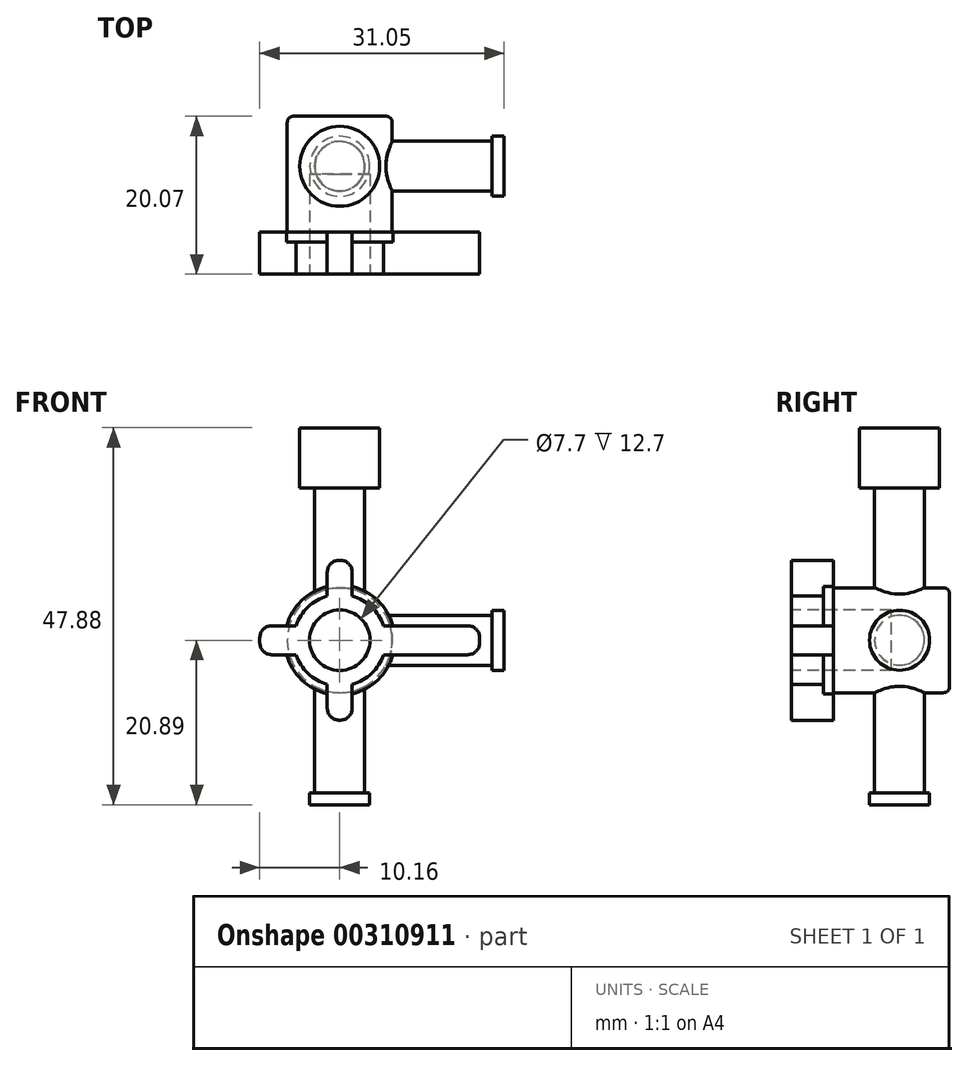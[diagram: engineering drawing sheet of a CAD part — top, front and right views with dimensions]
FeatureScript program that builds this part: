
annotation { "Feature Type Name" : "Feature", "Feature Type Description" : "" }
export const myFeature = defineFeature(function(context is Context, id is Id, definition is map)
    precondition{}
    {
        {
            var Q0;
            Q0=qCreatedBy(makeId("Front.planeOp"),FACE);
            var sketch = newSketch(context, id + "F0", { "sketchPlane" : qUnion([Q0])});
            skCircle(sketch, "E0", {"center": v(0, 0) * mm, "radius": 6.67 * mm});
            skSolve(sketch);
        }
        {
            var Q0;
            Q0 = qSketchRegion(id + "F0", true);
            extrude(context, id + "F1", {"entities" : qUnion([Q0]), "depth" : 14.73 * mm});
        }
        {
            var Q0;
            Q0=qCreatedBy(makeId("Top.planeOp"),FACE);
            var sketch = newSketch(context, id + "F2", { "sketchPlane" : qUnion([Q0])});
            skCircle(sketch, "E1", {"center": v(0, -6.35) * mm, "radius": 3.18 * mm});
            skSolve(sketch);
        }
        {
            var Q0;
            Q0 = qSketchRegion(id + "F2", true);
            extrude(context, id + "F3", {"entities" : qUnion([Q0]), "operationType" : NewBodyOperationType.ADD, "endBound" : BoundingType.SYMMETRIC, "depth" : 38.73 * mm});
        }
        {
            var Q0;
            Q0=qCreatedBy(makeId("Right.planeOp"),FACE);
            var sketch = newSketch(context, id + "F4", { "sketchPlane" : qUnion([Q0])});
            skCircle(sketch, "E2", {"center": v(-6.35, 0) * mm, "radius": 3.18 * mm});
            skSolve(sketch);
        }
        {
            var Q0;
            Q0 = qSketchRegion(id + "F4", true);
            extrude(context, id + "F5", {"entities" : qUnion([Q0]), "operationType" : NewBodyOperationType.ADD, "depth" : 19.37 * mm});
        }
        {
            var Q0;
            Q0=makeQuery(id+"F1.opExtrude","CAP_EDGE",EDGE,{"disambiguationData":[OSD([sQuery(id+"F0.wireOp",EDGE,"E0")])],"isStart":true});
            fillet(context, id + "F6", {"entities" : qUnion([Q0]), "radius" : 0.76 * mm, "tangentPropagation" : true, "allowEdgeOverflow" : false});
        }
        {
            var Q0;
            Q0=makeQuery(id+"F3.opExtrude","CAP_FACE",FACE,{"disambiguationData":[OSD([sQuery(id+"F2.wireOp",EDGE,"E1")])],"isStart":false});
            var sketch = newSketch(context, id + "F7", { "sketchPlane" : qUnion([Q0])});
            skCircle(sketch, "E3", {"center": v(0, -6.35) * mm, "radius": 5.08 * mm});
            skSolve(sketch);
        }
        {
            var Q0;
            Q0 = qSketchRegion(id + "F7", true);
            extrude(context, id + "F8", {"entities" : qUnion([Q0]), "operationType" : NewBodyOperationType.ADD, "depth" : 7.62 * mm});
        }
        {
            var Q0;
            Q0=makeQuery(id+"F5.opExtrude","CAP_FACE",FACE,{"disambiguationData":[OSD([sQuery(id+"F4.wireOp",EDGE,"E2")])],"isStart":false});
            var sketch = newSketch(context, id + "F9", { "sketchPlane" : qUnion([Q0])});
            skCircle(sketch, "E4", {"center": v(-6.35, 0) * mm, "radius": 3.81 * mm});
            skSolve(sketch);
        }
        {
            var Q0;
            Q0 = qSketchRegion(id + "F9", true);
            extrude(context, id + "F10", {"entities" : qUnion([Q0]), "operationType" : NewBodyOperationType.ADD, "depth" : 1.52 * mm});
        }
        {
            var Q0;
            Q0=makeQuery(id+"F3.opExtrude","CAP_FACE",FACE,{"disambiguationData":[OSD([sQuery(id+"F2.wireOp",EDGE,"E1")])],"isStart":true});
            var sketch = newSketch(context, id + "F11", { "sketchPlane" : qUnion([Q0])});
            skCircle(sketch, "E5", {"center": v(0, 6.35) * mm, "radius": 3.81 * mm});
            skSolve(sketch);
        }
        {
            var Q0;
            Q0 = qSketchRegion(id + "F11", true);
            extrude(context, id + "F12", {"entities" : qUnion([Q0]), "operationType" : NewBodyOperationType.ADD, "depth" : 1.52 * mm});
        }
        {
            var Q0;
            Q0=makeQuery(id+"F1.opExtrude","CAP_FACE",FACE,{"disambiguationData":[OSD([sQuery(id+"F0.wireOp",EDGE,"E0")])],"isStart":false});
            var sketch = newSketch(context, id + "F13", { "sketchPlane" : qUnion([Q0])});
            skCircle(sketch, "E6", {"center": v(0, 0) * mm, "radius": 6.99 * mm});
            skSolve(sketch);
        }
        {
            var Q0;
            Q0 = qSketchRegion(id + "F13", true);
            extrude(context, id + "F14", {"entities" : qUnion([Q0]), "depth" : 1.27 * mm});
        }
        {
            var Q0;
            Q0=makeQuery(id+"F14.opExtrude","CAP_FACE",FACE,{"disambiguationData":[OSD([sQuery(id+"F13.wireOp",EDGE,"E6")])],"isStart":false});
            var sketch = newSketch(context, id + "F15", { "sketchPlane" : qUnion([Q0])});
            skCircle(sketch, "E7", {"center": v(0, 0) * mm, "radius": 5.84 * mm});
            skCircle(sketch, "E8", {"center": v(0, 0) * mm, "radius": 3.81 * mm});
            skSolve(sketch);
        }
        {
            var Q0;
            Q0 = qSketchRegion(id + "F15", true);
            extrude(context, id + "F16", {"entities" : qUnion([Q0]), "operationType" : NewBodyOperationType.ADD, "depth" : 4.06 * mm});
        }
        {
            var Q0;
            Q0=makeQuery(id+"F14.opExtrude","CAP_FACE",FACE,{"disambiguationData":[OSD([sQuery(id+"F13.wireOp",EDGE,"E6")])],"isStart":true});
            var sketch = newSketch(context, id + "F17", { "sketchPlane" : qUnion([Q0])});
            skLineSegment(sketch, "E9.bottom", {"start": v(1.59, 10.16) * mm, "end": v(-1.59, 10.16) * mm});
            skLineSegment(sketch, "E9.top", {"start": v(1.59, -10.16) * mm, "end": v(-1.59, -10.16) * mm});
            skLineSegment(sketch, "E9.left", {"start": v(1.59, 10.16) * mm, "end": v(1.59, -10.16) * mm});
            skLineSegment(sketch, "E9.right", {"start": v(-1.59, 10.16) * mm, "end": v(-1.59, -10.16) * mm});
            skPoint(sketch, "E9.middle", {"position": v(0, 0) * mm});
            skSolve(sketch);
        }
        {
            var Q0;
            Q0 = qSketchRegion(id + "F17", true);
            var Q1;
            Q1=makeQuery(id+"F16.opExtrude","CAP_FACE",FACE,{"disambiguationData":[OSD([sQuery(id+"F15.wireOp",EDGE,"E7"),sQuery(id+"F15.wireOp",EDGE,"E8")])],"isStart":false});
            extrude(context, id + "F18", {"entities" : qUnion([Q0]), "operationType" : NewBodyOperationType.ADD, "endBound" : BoundingType.UP_TO_SURFACE, "oppositeDirection" : true, "endBoundEntityFace" : qUnion([Q1]), "depth" : 25.4 * mm});
        }
        {
            var Q0;
            Q0=makeQuery(id+"F18.boolean.opBoolean","MERGE",FACE,{"derivedFrom":[makeQuery(id+"F14.opExtrude","CAP_FACE",FACE,{"disambiguationData":[OSD([sQuery(id+"F13.wireOp",EDGE,"E6")])],"isStart":true}),makeQuery(id+"F18.opExtrude","CAP_FACE",FACE,{"disambiguationData":[OSD([sQuery(id+"F17.wireOp",EDGE,"E9.bottom"),sQuery(id+"F17.wireOp",EDGE,"E9.top"),sQuery(id+"F17.wireOp",EDGE,"E9.left"),sQuery(id+"F17.wireOp",EDGE,"E9.right")])],"isStart":true})]});
            var sketch = newSketch(context, id + "F19", { "sketchPlane" : qUnion([Q0])});
            skLineSegment(sketch, "E10.bottom", {"start": v(-17.78, 1.84) * mm, "end": v(10.16, 1.84) * mm});
            skLineSegment(sketch, "E10.top", {"start": v(-17.78, -1.84) * mm, "end": v(10.16, -1.84) * mm});
            skLineSegment(sketch, "E10.left", {"start": v(-17.78, 1.84) * mm, "end": v(-17.78, -1.84) * mm});
            skLineSegment(sketch, "E10.right", {"start": v(10.16, 1.84) * mm, "end": v(10.16, -1.84) * mm});
            skPoint(sketch, "E10.middle", {"position": v(-3.81, 0) * mm});
            skPoint(sketch, "E10.middle.positionSnap0", {"position": v(-6.99, 0) * mm});
            skPoint(sketch, "E10.centerSnap0", {"position": v(-6.99, 0) * mm});
            skSolve(sketch);
        }
        {
            var Q0;
            Q0 = qSketchRegion(id + "F19", true);
            var Q1;
            {var subQ0=sQuery(id+"F15.wireOp",EDGE,"E8");var subQ1=sQuery(id+"F15.wireOp",EDGE,"E7");Q1=makeQuery(id+"F18.boolean.opBoolean","MERGE",FACE,{"derivedFrom":[makeQuery(id+"F16.opExtrude","CAP_FACE",FACE,{"disambiguationData":[OSD([subQ1,subQ0])],"isStart":false}),makeQuery(id+"F18.opExtrude","CAP_FACE",FACE,{"disambiguationData":[OSD([subQ1,subQ0])],"isStart":false})]});}
            extrude(context, id + "F20", {"entities" : qUnion([Q0]), "operationType" : NewBodyOperationType.ADD, "endBound" : BoundingType.UP_TO_SURFACE, "oppositeDirection" : true, "endBoundEntityFace" : qUnion([Q1]), "depth" : 25.4 * mm});
        }
        {
            var Q0;
            {var subQ0=sQuery(id+"F15.wireOp",EDGE,"E8");var subQ1=sQuery(id+"F15.wireOp",EDGE,"E7");Q0=makeQuery(id+"F20.boolean.opBoolean","MERGE",FACE,{"derivedFrom":[makeQuery(id+"F18.boolean.opBoolean","MERGE",FACE,{"derivedFrom":[makeQuery(id+"F16.opExtrude","CAP_FACE",FACE,{"disambiguationData":[OSD([subQ1,subQ0])],"isStart":false}),makeQuery(id+"F18.opExtrude","CAP_FACE",FACE,{"disambiguationData":[OSD([subQ1,subQ0])],"isStart":false})]}),makeQuery(id+"F20.opExtrude","CAP_FACE",FACE,{"disambiguationData":[OSD([subQ1,subQ0])],"isStart":false})]});}
            var sketch = newSketch(context, id + "F21", { "sketchPlane" : qUnion([Q0])});
            skCircle(sketch, "E11", {"center": v(0, 0) * mm, "radius": 3.85 * mm});
            skSolve(sketch);
        }
        {
            var Q0;
            Q0 = qSketchRegion(id + "F21", true);
            extrude(context, id + "F22", {"entities" : qUnion([Q0]), "operationType" : NewBodyOperationType.REMOVE, "oppositeDirection" : true, "depth" : 12.7 * mm});
        }
        {
            var Q0;
            Q0=makeQuery(id+"F20.opExtrude","SWEPT_EDGE",EDGE,{"disambiguationData":[OSD([sQuery(id+"F19.wireOp",EDGE,"E10.top"),sQuery(id+"F19.wireOp",EDGE,"E10.left")])]});
            var Q1;
            Q1=makeQuery(id+"F20.opExtrude","SWEPT_EDGE",EDGE,{"disambiguationData":[OSD([sQuery(id+"F19.wireOp",EDGE,"E10.bottom"),sQuery(id+"F19.wireOp",EDGE,"E10.left")])]});
            var Q2;
            Q2=makeQuery(id+"F18.opExtrude","SWEPT_EDGE",EDGE,{"disambiguationData":[OSD([sQuery(id+"F17.wireOp",EDGE,"E9.bottom"),sQuery(id+"F17.wireOp",EDGE,"E9.right")])]});
            var Q3;
            Q3=makeQuery(id+"F18.opExtrude","SWEPT_EDGE",EDGE,{"disambiguationData":[OSD([sQuery(id+"F17.wireOp",EDGE,"E9.bottom"),sQuery(id+"F17.wireOp",EDGE,"E9.left")])]});
            var Q4;
            Q4=makeQuery(id+"F20.opExtrude","SWEPT_EDGE",EDGE,{"disambiguationData":[OSD([sQuery(id+"F19.wireOp",EDGE,"E10.bottom"),sQuery(id+"F19.wireOp",EDGE,"E10.right")])]});
            var Q5;
            Q5=makeQuery(id+"F20.opExtrude","SWEPT_EDGE",EDGE,{"disambiguationData":[OSD([sQuery(id+"F19.wireOp",EDGE,"E10.top"),sQuery(id+"F19.wireOp",EDGE,"E10.right")])]});
            var Q6;
            Q6=makeQuery(id+"F18.opExtrude","SWEPT_EDGE",EDGE,{"disambiguationData":[OSD([sQuery(id+"F17.wireOp",EDGE,"E9.top"),sQuery(id+"F17.wireOp",EDGE,"E9.left")])]});
            var Q7;
            Q7=makeQuery(id+"F18.opExtrude","SWEPT_EDGE",EDGE,{"disambiguationData":[OSD([sQuery(id+"F17.wireOp",EDGE,"E9.top"),sQuery(id+"F17.wireOp",EDGE,"E9.right")])]});
            fillet(context, id + "F23", {"entities" : qUnion([Q0, Q1, Q2, Q3, Q4, Q5, Q6, Q7]), "radius" : 1.52 * mm, "tangentPropagation" : true, "allowEdgeOverflow" : false});
        }
    });
